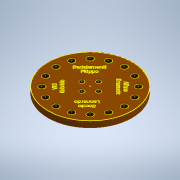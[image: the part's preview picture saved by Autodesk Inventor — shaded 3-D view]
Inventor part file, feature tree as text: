
AUTODESK INVENTOR PART (.ipt)
format: ipt  version: 2020.2 (Build 242310000, 310)  size: 1,739,776 bytes
history: native  units: mm
features: sketch x5, extrude x2, hole x2, other x1
ambient origin geometry x8: Origin, YZ Plane, XZ Plane, XY Plane, X Axis, Y Axis, Z Axis, Center Point
bodies: Solido1 (feature_tree)
feature tree (10):
  extrude  "Estrusione1"  Depth=80.0mm
  hole  "Foro1"  [1 undecoded]
  hole  "Foro2"  [1 undecoded]
  extrude  "Estrusione2"  TaperAngle=90.0deg  [1 undecoded]
  sketch  "Schizzo5"
  sketch  "Schizzo1"
  sketch  "Schizzo2"
  sketch  "Schizzo3"
  sketch  "Schizzo4"
  other  "Proietta spigoli di taglio1"
note: 3 required parameter values undecoded (feature->parameter linkage not recoverable at this tier; creation-order binding heuristic only, values carry confidence <= 0.55)
